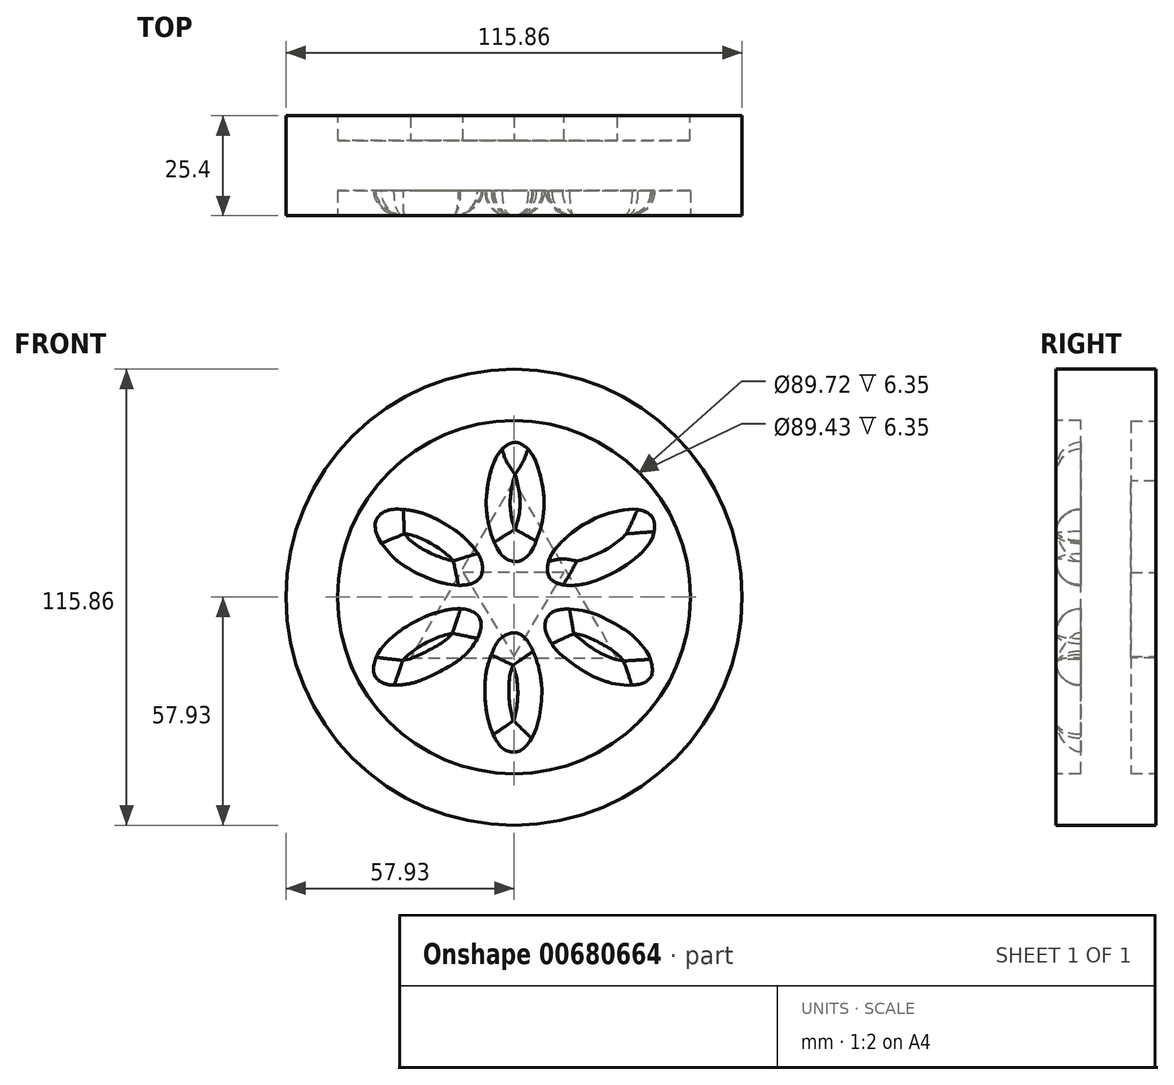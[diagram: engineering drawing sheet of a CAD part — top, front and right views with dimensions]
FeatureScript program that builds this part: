
annotation { "Feature Type Name" : "Feature", "Feature Type Description" : "" }
export const myFeature = defineFeature(function(context is Context, id is Id, definition is map)
    precondition{}
    {
        {
            var Q0;
            Q0=qCreatedBy(makeId("Front.planeOp"),FACE);
            var sketch = newSketch(context, id + "F0", { "sketchPlane" : qUnion([Q0])});
            skCircle(sketch, "E0", {"center": v(0, 0) * mm, "radius": 57.93 * mm});
            skCircle(sketch, "E1", {"center": v(0, 0) * mm, "radius": 45.24 * mm});
            skLineSegment(sketch, "E2", {"start": v(-24.01, 26.9) * mm, "end": v(-4.53, 1.77) * mm});
            skLineSegment(sketch, "E3", {"start": v(-4.53, 1.77) * mm, "end": v(-36.03, 4.88) * mm});
            skLineSegment(sketch, "E4", {"start": v(-36.03, 4.88) * mm, "end": v(-24.01, 26.9) * mm});
            skCircle(sketch, "E5", {"center": v(0, 29.6) * mm, "radius": 10.34 * mm});
            skLineSegment(sketch, "E6", {"start": v(4.46, 1.76) * mm, "end": v(24, 26.88) * mm});
            skLineSegment(sketch, "E7", {"start": v(24, 26.88) * mm, "end": v(36.16, 4.84) * mm});
            skLineSegment(sketch, "E8", {"start": v(36.16, 4.84) * mm, "end": v(4.46, 1.76) * mm});
            skLineSegment(sketch, "E9", {"start": v(0, -5.39) * mm, "end": v(12.64, -34.5) * mm});
            skLineSegment(sketch, "E10", {"start": v(12.64, -34.5) * mm, "end": v(-12.54, -34.5) * mm});
            skLineSegment(sketch, "E11", {"start": v(-12.54, -34.5) * mm, "end": v(0, -5.39) * mm});
            skCircle(sketch, "E12", {"center": v(-26.13, -15.37) * mm, "radius": 10.23 * mm});
            skCircle(sketch, "E13", {"center": v(26.13, -15.19) * mm, "radius": 9.93 * mm});
            skSolve(sketch);
        }
        {
            var Q0;
            Q0=makeQuery(id+"F0.imprint","IMPRINT",FACE,{"disambiguationData":[TD([[makeQuery(id+"F0.imprint","IMPRINT",EDGE,{"derivedFrom":sQuery(id+"F0.wireOp",EDGE,"E0")}),1.0]])]});
            var Q1;
            Q1=makeQuery(id+"F0.imprint","IMPRINT",FACE,{"disambiguationData":[TD([[makeQuery(id+"F0.imprint","IMPRINT",EDGE,{"derivedFrom":sQuery(id+"F0.wireOp",EDGE,"E1")}),1.0]])]});
            var Q2;
            Q2=makeQuery(id+"F0.imprint","IMPRINT",FACE,{"disambiguationData":[TD([[makeQuery(id+"F0.imprint","IMPRINT",EDGE,{"derivedFrom":sQuery(id+"F0.wireOp",EDGE,"E5")}),1.0]])]});
            var Q3;
            Q3=makeQuery(id+"F0.imprint","IMPRINT",FACE,{"disambiguationData":[TD([[makeQuery(id+"F0.imprint","IMPRINT",EDGE,{"derivedFrom":sQuery(id+"F0.wireOp",EDGE,"E2")}),-1.0]])]});
            var Q4;
            Q4=makeQuery(id+"F0.imprint","IMPRINT",FACE,{"disambiguationData":[TD([[makeQuery(id+"F0.imprint","IMPRINT",EDGE,{"derivedFrom":sQuery(id+"F0.wireOp",EDGE,"E12")}),1.0]])]});
            var Q5;
            Q5=makeQuery(id+"F0.imprint","IMPRINT",FACE,{"disambiguationData":[TD([[makeQuery(id+"F0.imprint","IMPRINT",EDGE,{"derivedFrom":sQuery(id+"F0.wireOp",EDGE,"E9")}),-1.0]])]});
            var Q6;
            Q6=makeQuery(id+"F0.imprint","IMPRINT",FACE,{"disambiguationData":[TD([[makeQuery(id+"F0.imprint","IMPRINT",EDGE,{"derivedFrom":sQuery(id+"F0.wireOp",EDGE,"E13")}),1.0]])]});
            var Q7;
            Q7=makeQuery(id+"F0.imprint","IMPRINT",FACE,{"disambiguationData":[TD([[makeQuery(id+"F0.imprint","IMPRINT",EDGE,{"derivedFrom":sQuery(id+"F0.wireOp",EDGE,"E6")}),-1.0]])]});
            extrude(context, id + "F1", {"entities" : qUnion([Q0, Q1, Q2, Q3, Q4, Q5, Q6, Q7]), "depth" : 12.7 * mm, "offsetDistance" : 25.4 * mm});
        }
        {
            var Q0;
            Q0=makeQuery(id+"F1.opExtrude","CAP_FACE",FACE,{"disambiguationData":[OSD([sQuery(id+"F0.wireOp",EDGE,"E0")])],"isStart":true});
            extrude(context, id + "F2", {"entities" : qUnion([Q0]), "operationType" : NewBodyOperationType.ADD, "depth" : 12.7 * mm, "offsetDistance" : 25.4 * mm});
        }
        {
            var Q0;
            Q0=makeQuery(id+"F1.opExtrude","CAP_FACE",FACE,{"disambiguationData":[OSD([sQuery(id+"F0.wireOp",EDGE,"E0")])],"isStart":false});
            var sketch = newSketch(context, id + "F3", { "sketchPlane" : qUnion([Q0])});
            skCircle(sketch, "E14", {"center": v(0, 0) * mm, "radius": 44.86 * mm});
            skSolve(sketch);
        }
        {
            var Q0;
            Q0=makeQuery(id+"F3.imprint","IMPRINT",FACE,{"disambiguationData":[TD([[makeQuery(id+"F3.imprint","IMPRINT",EDGE,{"derivedFrom":sQuery(id+"F3.wireOp",EDGE,"E14")}),1.0]])]});
            extrude(context, id + "F4", {"entities" : qUnion([Q0]), "operationType" : NewBodyOperationType.REMOVE, "oppositeDirection" : true, "depth" : 6.35 * mm, "offsetDistance" : 25.4 * mm});
        }
        {
            var Q0;
            Q0=makeQuery(id+"F2.opExtrude","CAP_FACE",FACE,{"disambiguationData":[OSD([sQuery(id+"F0.wireOp",EDGE,"E0")])],"isStart":false});
            var sketch = newSketch(context, id + "F5", { "sketchPlane" : qUnion([Q0])});
            skCircle(sketch, "E15", {"center": v(0, 0) * mm, "radius": 44.72 * mm});
            skSolve(sketch);
        }
        {
            var Q0;
            Q0=makeQuery(id+"F5.imprint","IMPRINT",FACE,{"disambiguationData":[TD([[makeQuery(id+"F5.imprint","IMPRINT",EDGE,{"derivedFrom":sQuery(id+"F5.wireOp",EDGE,"E15")}),1.0]])]});
            extrude(context, id + "F6", {"entities" : qUnion([Q0]), "operationType" : NewBodyOperationType.REMOVE, "oppositeDirection" : true, "depth" : 6.35 * mm, "offsetDistance" : 25.4 * mm});
        }
        {
            var Q0;
            Q0=makeQuery(id+"F6.boolean.opBoolean","COPY",FACE,{"derivedFrom":makeQuery(id+"F6.opExtrude","CAP_FACE",FACE,{"disambiguationData":[OSD([sQuery(id+"F5.wireOp",EDGE,"E15")])],"isStart":false})});
            var sketch = newSketch(context, id + "F7", { "sketchPlane" : qUnion([Q0])});
            skLineSegment(sketch, "E16", {"start": v(0, 29.52) * mm, "end": v(26.34, -15.44) * mm});
            skLineSegment(sketch, "E17", {"start": v(26.34, -15.44) * mm, "end": v(-26.11, -15.44) * mm});
            skLineSegment(sketch, "E18", {"start": v(-26.11, -15.44) * mm, "end": v(0, 29.52) * mm});
            skLineSegment(sketch, "E19", {"start": v(13.17, 7.04) * mm, "end": v(0.11, -15.44) * mm});
            skLineSegment(sketch, "E20", {"start": v(0.11, -15.44) * mm, "end": v(-13.06, 7.04) * mm});
            skLineSegment(sketch, "E21", {"start": v(-13.06, 7.04) * mm, "end": v(13.17, 7.04) * mm});
            skSolve(sketch);
        }
        {
            var Q0;
            {var subQ3=sQuery(id+"F7.wireOp",EDGE,"E20");Q0=makeQuery(id+"F7.imprint","IMPRINT",FACE,{"disambiguationData":[TD([[makeQuery(id+"F7.imprint","IMPRINT",EDGE,{"derivedFrom":subQ3}),1.0]])]});}
            var Q1;
            Q1=makeQuery(id+"F7.imprint","IMPRINT",FACE,{"disambiguationData":[TD([[makeQuery(id+"F7.imprint","IMPRINT",EDGE,{"derivedFrom":sQuery(id+"F7.wireOp",EDGE,"E19")}),-1.0]])]});
            var Q2;
            {var subQ3=sQuery(id+"F7.wireOp",EDGE,"E21");Q2=makeQuery(id+"F7.imprint","IMPRINT",FACE,{"disambiguationData":[TD([[makeQuery(id+"F7.imprint","IMPRINT",EDGE,{"derivedFrom":subQ3}),1.0]])]});}
            var Q3;
            {var subQ3=sQuery(id+"F7.wireOp",EDGE,"E19");Q3=makeQuery(id+"F7.imprint","IMPRINT",FACE,{"disambiguationData":[TD([[makeQuery(id+"F7.imprint","IMPRINT",EDGE,{"derivedFrom":subQ3}),1.0]])]});}
            extrude(context, id + "F8", {"entities" : qUnion([Q0, Q1, Q2, Q3]), "operationType" : NewBodyOperationType.ADD, "depth" : 6.35 * mm, "offsetDistance" : 25.4 * mm});
        }
        {
            var Q0;
            Q0=makeQuery(id+"F8.opExtrude","CAP_FACE",FACE,{"disambiguationData":[OSD([sQuery(id+"F7.wireOp",EDGE,"E16"),sQuery(id+"F7.wireOp",EDGE,"E17"),sQuery(id+"F7.wireOp",EDGE,"E18")])],"isStart":false});
            var sketch = newSketch(context, id + "F9", { "sketchPlane" : qUnion([Q0])});
            skLineSegment(sketch, "E22", {"start": v(-12.72, 6.35) * mm, "end": v(12.98, 6.35) * mm});
            skLineSegment(sketch, "E23", {"start": v(12.98, 6.35) * mm, "end": v(0, -15) * mm});
            skLineSegment(sketch, "E24", {"start": v(0, -15) * mm, "end": v(-12.72, 6.35) * mm});
            skSolve(sketch);
        }
        {
            var Q0;
            Q0=makeQuery(id+"F9.imprint","IMPRINT",FACE,{"disambiguationData":[TD([[makeQuery(id+"F9.imprint","IMPRINT",EDGE,{"derivedFrom":sQuery(id+"F9.wireOp",EDGE,"E22")}),-1.0]])]});
            extrude(context, id + "F10", {"entities" : qUnion([Q0]), "operationType" : NewBodyOperationType.REMOVE, "oppositeDirection" : true, "depth" : 6.35 * mm, "offsetDistance" : 25.4 * mm});
        }
        {
            var Q0;
            Q0=makeQuery(id+"F4.boolean.opBoolean","COPY",FACE,{"derivedFrom":makeQuery(id+"F4.opExtrude","CAP_FACE",FACE,{"disambiguationData":[OSD([sQuery(id+"F3.wireOp",EDGE,"E14")])],"isStart":false})});
            var sketch = newSketch(context, id + "F11", { "sketchPlane" : qUnion([Q0])});
            skFitSpline(sketch, "E25", {"points": [v(0, 39.35) * mm, v(2.27, 38.65) * mm, v(4.25, 36.76) * mm, v(5.75, 33.94) * mm, v(7.07, 29.14) * mm, v(7.63, 24.2) * mm, v(7.02, 18.6) * mm, v(5.1, 13.06) * mm, v(3.4, 10.42) * mm, v(1.33, 9.15) * mm, v(-0.5, 9.15) * mm, v(-2.43, 10.05) * mm, v(-4.32, 12.54) * mm, v(-6.06, 16.87) * mm, v(-7.04, 22.93) * mm, v(-6.48, 29.52) * mm, v(-4.97, 34.55) * mm, v(-3, 37.61) * mm, v(0, 39.35) * mm]});
            skFitSpline(sketch, "E26", {"points": [v(35.08, 20.42) * mm, v(35.7, 17.83) * mm, v(34.45, 13.77) * mm, v(29.33, 8.73) * mm, v(24.01, 5.58) * mm, v(18.1, 3.44) * mm, v(13.4, 3.02) * mm, v(10.8, 3.65) * mm, v(8.92, 5.2) * mm, v(8.6, 8.24) * mm, v(9.76, 11.21) * mm, v(12.1, 14.02) * mm, v(14.87, 16.5) * mm, v(18.62, 18.95) * mm, v(22.01, 20.63) * mm, v(25.3, 21.65) * mm, v(28.42, 22.25) * mm, v(31.43, 22.28) * mm, v(33.47, 21.65) * mm, v(35.08, 20.42) * mm]});
            skFitSpline(sketch, "E27", {"points": [v(8.96, -4.44) * mm, v(12.14, -3.1) * mm, v(16.4, -3.25) * mm, v(20.54, -4.27) * mm, v(25.15, -6.49) * mm, v(29.42, -9.19) * mm, v(32.56, -12.33) * mm, v(34.47, -15.34) * mm, v(35.05, -19.4) * mm, v(33.48, -21.52) * mm, v(30.51, -22.3) * mm, v(26.79, -22.2) * mm, v(22.52, -21.14) * mm, v(17.12, -18.44) * mm, v(12.89, -15.34) * mm, v(10.46, -13.08) * mm, v(8.55, -9.94) * mm, v(7.83, -7.34) * mm, v(8.96, -4.44) * mm]});
            skFitSpline(sketch, "E28", {"points": [v(0, -9.06) * mm, v(3, -10.6) * mm, v(6.01, -16.94) * mm, v(7.03, -22.88) * mm, v(6.68, -29.03) * mm, v(4.86, -35.23) * mm, v(2.07, -38.69) * mm, v(0, -39.35) * mm, v(-2.67, -38.56) * mm, v(-4.97, -35.54) * mm, v(-6.65, -30.72) * mm, v(-7.32, -25.93) * mm, v(-7.36, -21.81) * mm, v(-6.79, -17.65) * mm, v(-5.5, -13.93) * mm, v(-3.51, -10.6) * mm, v(0, -9.06) * mm]});
            skFitSpline(sketch, "E29", {"points": [v(-23.99, -21.23) * mm, v(-14.9, -16.6) * mm, v(-10.43, -12.3) * mm, v(-8.46, -8.17) * mm, v(-8.7, -5.36) * mm, v(-10.62, -3.63) * mm, v(-13.66, -2.93) * mm, v(-17.24, -3.28) * mm, v(-22.33, -4.86) * mm, v(-26.99, -7.25) * mm, v(-30.57, -9.83) * mm, v(-33.96, -13.41) * mm, v(-35.5, -16.8) * mm, v(-35.58, -19.46) * mm, v(-34.12, -21.3) * mm, v(-31.19, -22.3) * mm, v(-27.5, -22.12) * mm, v(-23.99, -21.23) * mm]});
            skFitSpline(sketch, "E30", {"points": [v(-8.3, 5.66) * mm, v(-8.47, 9.66) * mm, v(-12.93, 15.37) * mm, v(-17.28, 18.47) * mm, v(-21.53, 20.68) * mm, v(-25.5, 21.93) * mm, v(-28.74, 22.32) * mm, v(-31.6, 22.18) * mm, v(-33.8, 21.15) * mm, v(-35.12, 19.22) * mm, v(-35.05, 16.61) * mm, v(-33.3, 13.26) * mm, v(-30.38, 9.87) * mm, v(-27.17, 7.48) * mm, v(-23.42, 5.52) * mm, v(-18.28, 3.63) * mm, v(-13.04, 3.05) * mm, v(-10, 3.8) * mm, v(-8.3, 5.66) * mm]});
            skSolve(sketch);
        }
        {
            var Q0;
            Q0=makeQuery(id+"F11.imprint","IMPRINT",FACE,{"disambiguationData":[TD([[makeQuery(id+"F11.imprint","IMPRINT",EDGE,{"derivedFrom":sQuery(id+"F11.wireOp",EDGE,"E25")}),-1.0]])]});
            var Q1;
            Q1=makeQuery(id+"F11.imprint","IMPRINT",FACE,{"disambiguationData":[TD([[makeQuery(id+"F11.imprint","IMPRINT",EDGE,{"derivedFrom":sQuery(id+"F11.wireOp",EDGE,"E26")}),-1.0]])]});
            var Q2;
            Q2=makeQuery(id+"F11.imprint","IMPRINT",FACE,{"disambiguationData":[TD([[makeQuery(id+"F11.imprint","IMPRINT",EDGE,{"derivedFrom":sQuery(id+"F11.wireOp",EDGE,"E27")}),-1.0]])]});
            var Q3;
            Q3=makeQuery(id+"F11.imprint","IMPRINT",FACE,{"disambiguationData":[TD([[makeQuery(id+"F11.imprint","IMPRINT",EDGE,{"derivedFrom":sQuery(id+"F11.wireOp",EDGE,"E28")}),-1.0]])]});
            var Q4;
            Q4=makeQuery(id+"F11.imprint","IMPRINT",FACE,{"disambiguationData":[TD([[makeQuery(id+"F11.imprint","IMPRINT",EDGE,{"derivedFrom":sQuery(id+"F11.wireOp",EDGE,"E29")}),1.0]])]});
            var Q5;
            Q5=makeQuery(id+"F11.imprint","IMPRINT",FACE,{"disambiguationData":[TD([[makeQuery(id+"F11.imprint","IMPRINT",EDGE,{"derivedFrom":sQuery(id+"F11.wireOp",EDGE,"E30")}),1.0]])]});
            extrude(context, id + "F12", {"entities" : qUnion([Q0, Q1, Q2, Q3, Q4, Q5]), "operationType" : NewBodyOperationType.ADD, "depth" : 6.35 * mm, "offsetDistance" : 25.4 * mm});
        }
        {
            var Q0;
            Q0=makeQuery(id+"F12.opExtrude","CAP_FACE",FACE,{"disambiguationData":[OSD([sQuery(id+"F11.wireOp",EDGE,"E25")])],"isStart":false});
            fillet(context, id + "F13", {"entities" : qUnion([Q0]), "radius" : 6.1 * mm, "tangentPropagation" : true, "allowEdgeOverflow" : false});
        }
        {
            var Q0;
            Q0=makeQuery(id+"F12.opExtrude","CAP_FACE",FACE,{"disambiguationData":[OSD([sQuery(id+"F11.wireOp",EDGE,"E26")])],"isStart":false});
            fillet(context, id + "F14", {"entities" : qUnion([Q0]), "radius" : 6.1 * mm, "tangentPropagation" : true, "allowEdgeOverflow" : false});
        }
        {
            var Q0;
            Q0=makeQuery(id+"F12.opExtrude","CAP_FACE",FACE,{"disambiguationData":[OSD([sQuery(id+"F11.wireOp",EDGE,"E27")])],"isStart":false});
            fillet(context, id + "F15", {"entities" : qUnion([Q0]), "radius" : 6.1 * mm, "tangentPropagation" : true, "allowEdgeOverflow" : false});
        }
        {
            var Q0;
            Q0=makeQuery(id+"F12.opExtrude","CAP_FACE",FACE,{"disambiguationData":[OSD([sQuery(id+"F11.wireOp",EDGE,"E28")])],"isStart":false});
            fillet(context, id + "F16", {"entities" : qUnion([Q0]), "radius" : 6.1 * mm, "tangentPropagation" : true, "allowEdgeOverflow" : false});
        }
        {
            var Q0;
            Q0=makeQuery(id+"F12.opExtrude","CAP_FACE",FACE,{"disambiguationData":[OSD([sQuery(id+"F11.wireOp",EDGE,"E29")])],"isStart":false});
            fillet(context, id + "F17", {"entities" : qUnion([Q0]), "radius" : 6.1 * mm, "tangentPropagation" : true, "allowEdgeOverflow" : false});
        }
        {
            var Q0;
            Q0=makeQuery(id+"F12.opExtrude","CAP_FACE",FACE,{"disambiguationData":[OSD([sQuery(id+"F11.wireOp",EDGE,"E30")])],"isStart":false});
            fillet(context, id + "F18", {"entities" : qUnion([Q0]), "radius" : 6.1 * mm, "tangentPropagation" : true, "allowEdgeOverflow" : false});
        }
    });
